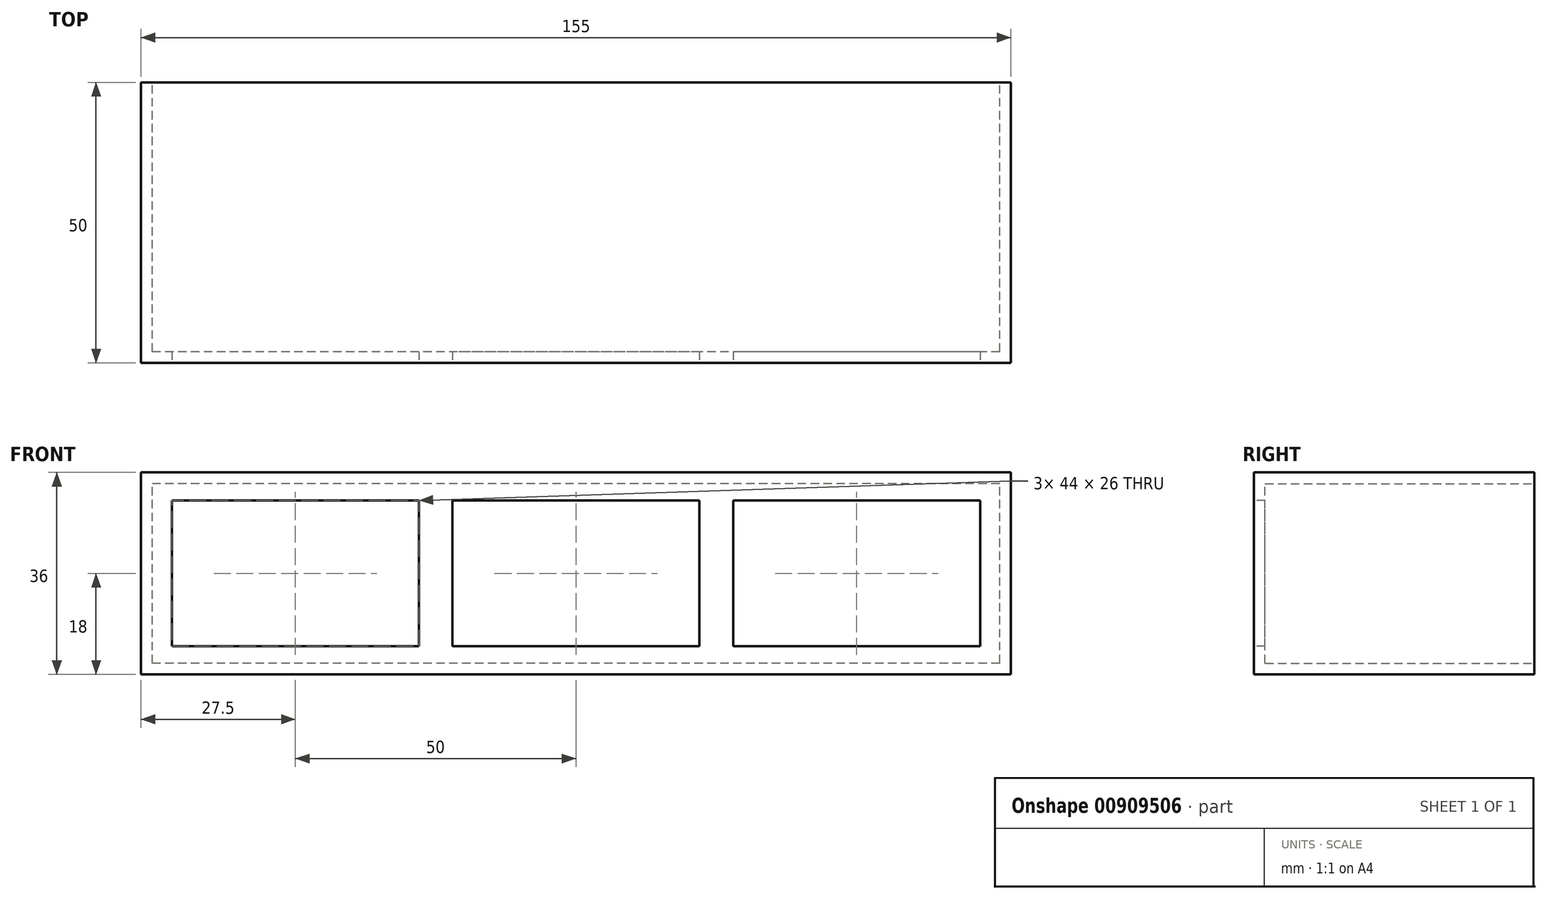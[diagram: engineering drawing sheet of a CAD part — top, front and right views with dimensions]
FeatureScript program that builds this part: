
annotation { "Feature Type Name" : "Feature", "Feature Type Description" : "" }
export const myFeature = defineFeature(function(context is Context, id is Id, definition is map)
    precondition{}
    {
        {
            var Q0;
            Q0=qCreatedBy(makeId("Front.planeOp"),FACE);
            var sketch = newSketch(context, id + "F0", { "sketchPlane" : qUnion([Q0])});
            skLineSegment(sketch, "E0.bottom", {"start": v(77.5, -18) * mm, "end": v(-77.5, -18) * mm});
            skLineSegment(sketch, "E0.top", {"start": v(77.5, 18) * mm, "end": v(-77.5, 18) * mm});
            skLineSegment(sketch, "E0.left", {"start": v(77.5, -18) * mm, "end": v(77.5, 18) * mm});
            skLineSegment(sketch, "E0.right", {"start": v(-77.5, -18) * mm, "end": v(-77.5, 18) * mm});
            skPoint(sketch, "E0.middle", {"position": v(0, 0) * mm});
            skSolve(sketch);
        }
        {
            var Q0;
            Q0 = qSketchRegion(id + "F0", true);
            extrude(context, id + "F1", {"entities" : qUnion([Q0]), "depth" : 50 * mm, "offsetDistance" : 25 * mm});
        }
        {
            var Q0;
            Q0=makeQuery(id+"F1.opExtrude","CAP_FACE",FACE,{"disambiguationData":[OSD([sQuery(id+"F0.wireOp",EDGE,"E0.bottom"),sQuery(id+"F0.wireOp",EDGE,"E0.top"),sQuery(id+"F0.wireOp",EDGE,"E0.left"),sQuery(id+"F0.wireOp",EDGE,"E0.right")])],"isStart":true});
            shell(context, id + "F2", {"entities" : qUnion([Q0]), "thickness" : 2 * mm});
        }
        {
            var Q0;
            Q0=makeQuery(id+"F1.opExtrude","CAP_FACE",FACE,{"disambiguationData":[OSD([sQuery(id+"F0.wireOp",EDGE,"E0.bottom"),sQuery(id+"F0.wireOp",EDGE,"E0.top"),sQuery(id+"F0.wireOp",EDGE,"E0.left"),sQuery(id+"F0.wireOp",EDGE,"E0.right")])],"isStart":false});
            var sketch = newSketch(context, id + "F3", { "sketchPlane" : qUnion([Q0])});
            skLineSegment(sketch, "E1", {"start": v(-77.5, 0) * mm, "end": v(77.5, 0) * mm, "construction": true});
            skPoint(sketch, "E1.startSnap0", {"position": v(-77.5, 0) * mm});
            skLineSegment(sketch, "E2", {"start": v(0, 18) * mm, "end": v(0, -18) * mm, "construction": true});
            skLineSegment(sketch, "E3.bottom", {"start": v(22, -13) * mm, "end": v(-22, -13) * mm});
            skLineSegment(sketch, "E3.top", {"start": v(22, 13) * mm, "end": v(-22, 13) * mm});
            skLineSegment(sketch, "E3.left", {"start": v(22, -13) * mm, "end": v(22, 13) * mm});
            skLineSegment(sketch, "E3.right", {"start": v(-22, -13) * mm, "end": v(-22, 13) * mm});
            skPoint(sketch, "E3.middle", {"position": v(0, 0) * mm});
            skLineSegment(sketch, "E4.bottom", {"start": v(-28, -13) * mm, "end": v(-72, -13) * mm});
            skLineSegment(sketch, "E4.top", {"start": v(-28, 13) * mm, "end": v(-72, 13) * mm});
            skLineSegment(sketch, "E4.left", {"start": v(-28, -13) * mm, "end": v(-28, 13) * mm});
            skLineSegment(sketch, "E4.right", {"start": v(-72, -13) * mm, "end": v(-72, 13) * mm});
            skPoint(sketch, "E4.middle", {"position": v(-50, 0) * mm});
            skLineSegment(sketch, "E5.bottom", {"start": v(72, -13) * mm, "end": v(28, -13) * mm});
            skLineSegment(sketch, "E5.top", {"start": v(72, 13) * mm, "end": v(28, 13) * mm});
            skLineSegment(sketch, "E5.left", {"start": v(72, -13) * mm, "end": v(72, 13) * mm});
            skLineSegment(sketch, "E5.right", {"start": v(28, -13) * mm, "end": v(28, 13) * mm});
            skPoint(sketch, "E5.middle", {"position": v(50, 0) * mm});
            skSolve(sketch);
        }
        {
            var Q0;
            Q0 = qSketchRegion(id + "F3", true);
            extrude(context, id + "F4", {"entities" : qUnion([Q0]), "operationType" : NewBodyOperationType.REMOVE, "oppositeDirection" : true, "depth" : 25 * mm, "offsetDistance" : 25 * mm});
        }
    });
